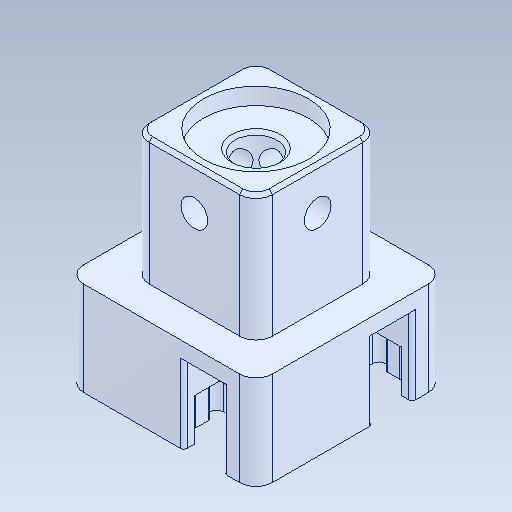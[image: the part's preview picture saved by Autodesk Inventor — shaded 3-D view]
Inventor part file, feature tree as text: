
AUTODESK INVENTOR PART (.ipt)
format: ipt  version: 2020 (Build 240168000, 168)  size: 236,544 bytes
history: native  units: in
note: dims shown in document units (in); Inventor stores cm internally (conversion verified against a paired STEP export)
features: fillet x1
ambient origin geometry x8: Origin, YZ Plane, XZ Plane, XY Plane, X Axis, Y Axis, Z Axis, Center Point
bodies: Solid1 (feature_tree)
feature tree (1):
  fillet  "Fillet11"  [1 undecoded]
note: 1 required parameter value undecoded (feature->parameter linkage not recoverable at this tier; creation-order binding heuristic only, values carry confidence <= 0.55)
